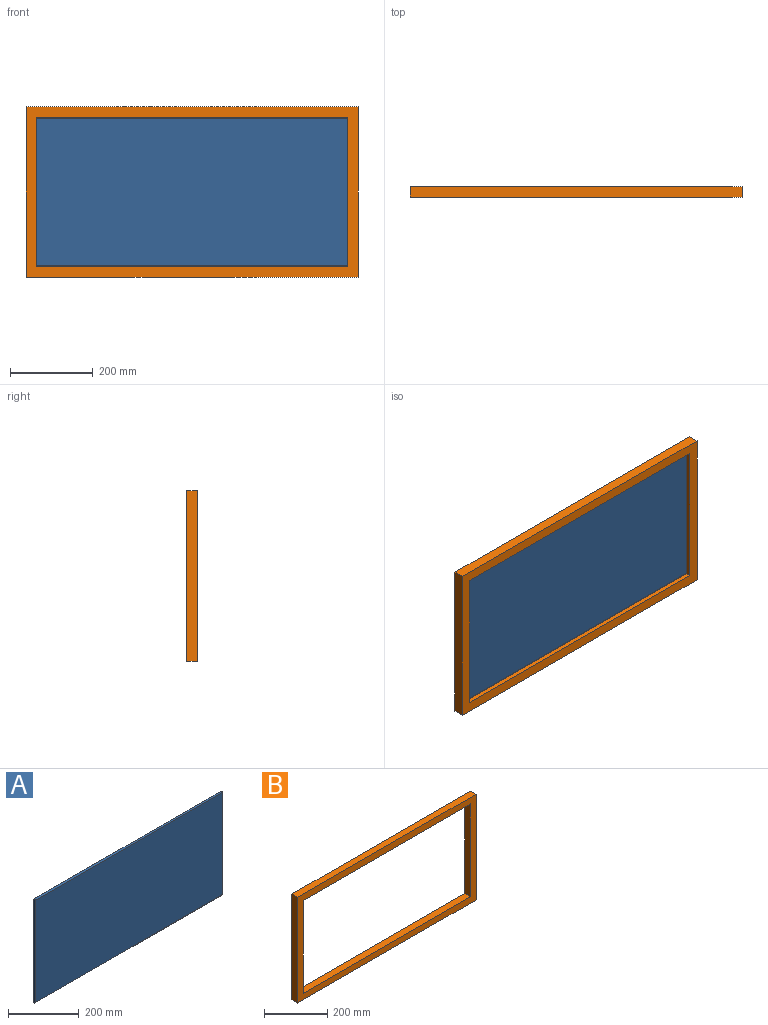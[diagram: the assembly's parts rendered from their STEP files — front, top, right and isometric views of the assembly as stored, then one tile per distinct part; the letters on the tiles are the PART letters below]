
ASSEMBLY  parts=2 mates=1
PART A: 6 faces, bbox 750x6x360 mm
  f0: plane 360x6mm, normal (-1,0,0), area 2152.3mm2, adj f2,f3,f4,f5
  f1: plane 360x6mm, normal (1,0,0), area 2152.3mm2, adj f2,f3,f4,f5
  f2: plane 750x354mm, normal (0,-1,0), area 265500mm2, adj f0,f1,f4,f5
  f3: plane 750x354mm, normal (0,1,0), area 265500mm2, adj f0,f1,f4,f5
  f4: cylinder r=3mm len=750mm, axis (-1,0,0), area 7068.6mm2, adj f0,f1,f2,f3
  f5: cylinder r=3mm len=750mm, axis (1,0,0), area 7068.6mm2, adj f0,f1,f2,f3
PART B: 10 faces, bbox 800x25x410 mm
  f0: plane 360x25mm, normal (1,0,0), area 9000mm2, adj f1,f7,f8,f9
  f1: plane 750x25mm, normal (0,0,-1), area 18750mm2, adj f0,f2,f8,f9
  f2: plane 360x25mm, normal (-1,0,0), area 9000mm2, adj f1,f7,f8,f9
  f3: plane 410x25mm, normal (-1,0,0), area 10250mm2, adj f4,f6,f8,f9
  f4: plane 800x25mm, normal (0,0,-1), area 20000mm2, adj f3,f5,f8,f9
  f5: plane 410x25mm, normal (1,0,0), area 10250mm2, adj f4,f6,f8,f9
  f6: plane 800x25mm, normal (0,0,1), area 20000mm2, adj f3,f5,f8,f9
  f7: plane 750x25mm, normal (0,0,1), area 18750mm2, adj f0,f2,f8,f9
  f8: plane 800x410mm, normal (0,-1,0), area 58000mm2, adj f0,f1,f2,f3,f4,f5,f6,f7
  f9: plane 800x410mm, normal (0,1,0), area 58000mm2, adj f0,f1,f2,f3,f4,f5,f6,f7
PLACE A at identity
PLACE B at identity fixed
MATE revolute B.f0 <-> A.f4  axis (-1,0,0) through (25,0,28)mm
